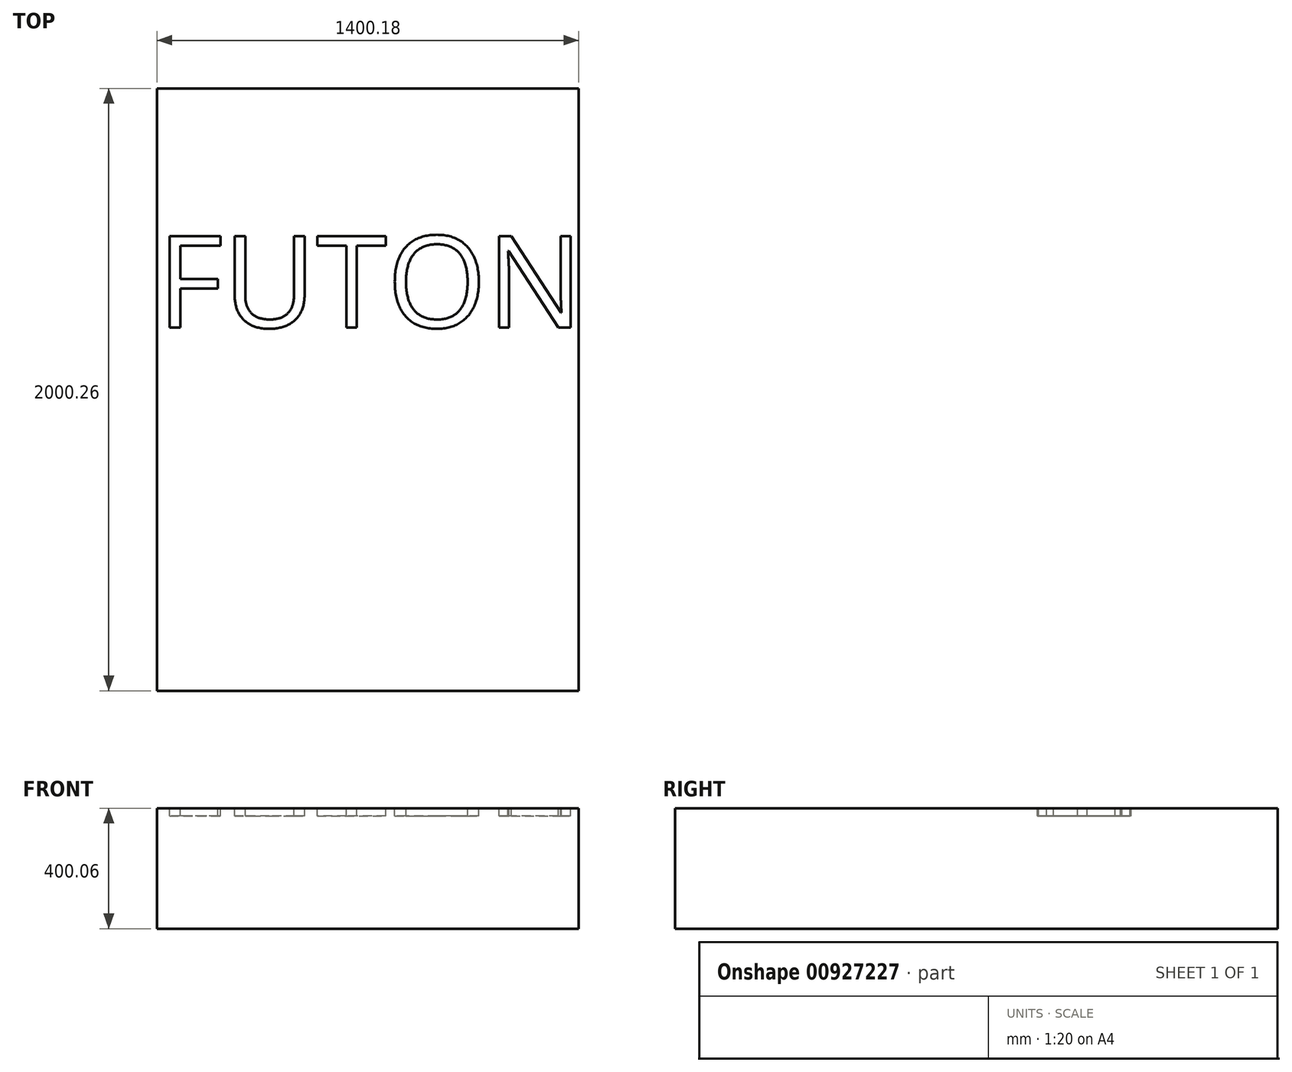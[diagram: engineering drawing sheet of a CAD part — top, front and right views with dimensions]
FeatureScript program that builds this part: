
annotation { "Feature Type Name" : "Feature", "Feature Type Description" : "" }
export const myFeature = defineFeature(function(context is Context, id is Id, definition is map)
    precondition{}
    {
        {
            var Q0;
            Q0=qCreatedBy(makeId("Top.planeOp"),FACE);
            var sketch = newSketch(context, id + "F0", { "sketchPlane" : qUnion([Q0])});
            skLineSegment(sketch, "E0.bottom", {"start": v(700.09, -1000.13) * mm, "end": v(-700.09, -1000.13) * mm});
            skLineSegment(sketch, "E0.top", {"start": v(700.09, 1000.13) * mm, "end": v(-700.09, 1000.13) * mm});
            skLineSegment(sketch, "E0.left", {"start": v(700.09, -1000.13) * mm, "end": v(700.09, 1000.13) * mm});
            skLineSegment(sketch, "E0.right", {"start": v(-700.09, -1000.13) * mm, "end": v(-700.09, 1000.12) * mm});
            skPoint(sketch, "E0.middle", {"position": v(0, 0) * mm});
            skSolve(sketch);
        }
        {
            var Q0;
            Q0 = qSketchRegion(id + "F0", true);
            extrude(context, id + "F1", {"entities" : qUnion([Q0]), "endBound" : BoundingType.SYMMETRIC, "depth" : 400.05 * mm, "offsetDistance" : 25.4 * mm});
        }
        {
            var Q0;
            Q0=makeQuery(id+"F1.opExtrude","CAP_FACE",FACE,{"disambiguationData":[OSD([sQuery(id+"F0.wireOp",EDGE,"E0.bottom"),sQuery(id+"F0.wireOp",EDGE,"E0.top"),sQuery(id+"F0.wireOp",EDGE,"E0.left"),sQuery(id+"F0.wireOp",EDGE,"E0.right")])],"isStart":false});
            var sketch = newSketch(context, id + "F2", { "sketchPlane" : qUnion([Q0])});
            skText(sketch, "E1", { "text": "FUTON", "fontName": "OpenSans-Regular.ttf"});
            const initialGuessF2  = {"E1": [-0.70009, 0.20577, 1, 0, 0.3058]};
            skSetInitialGuess(sketch, initialGuessF2);
            skSolve(sketch);
        }
        {
            var Q0;
            Q0 = qSketchRegion(id + "F2", true);
            extrude(context, id + "F3", {"entities" : qUnion([Q0]), "operationType" : NewBodyOperationType.REMOVE, "oppositeDirection" : true, "depth" : 25.4 * mm, "offsetDistance" : 25.4 * mm});
        }
    });
